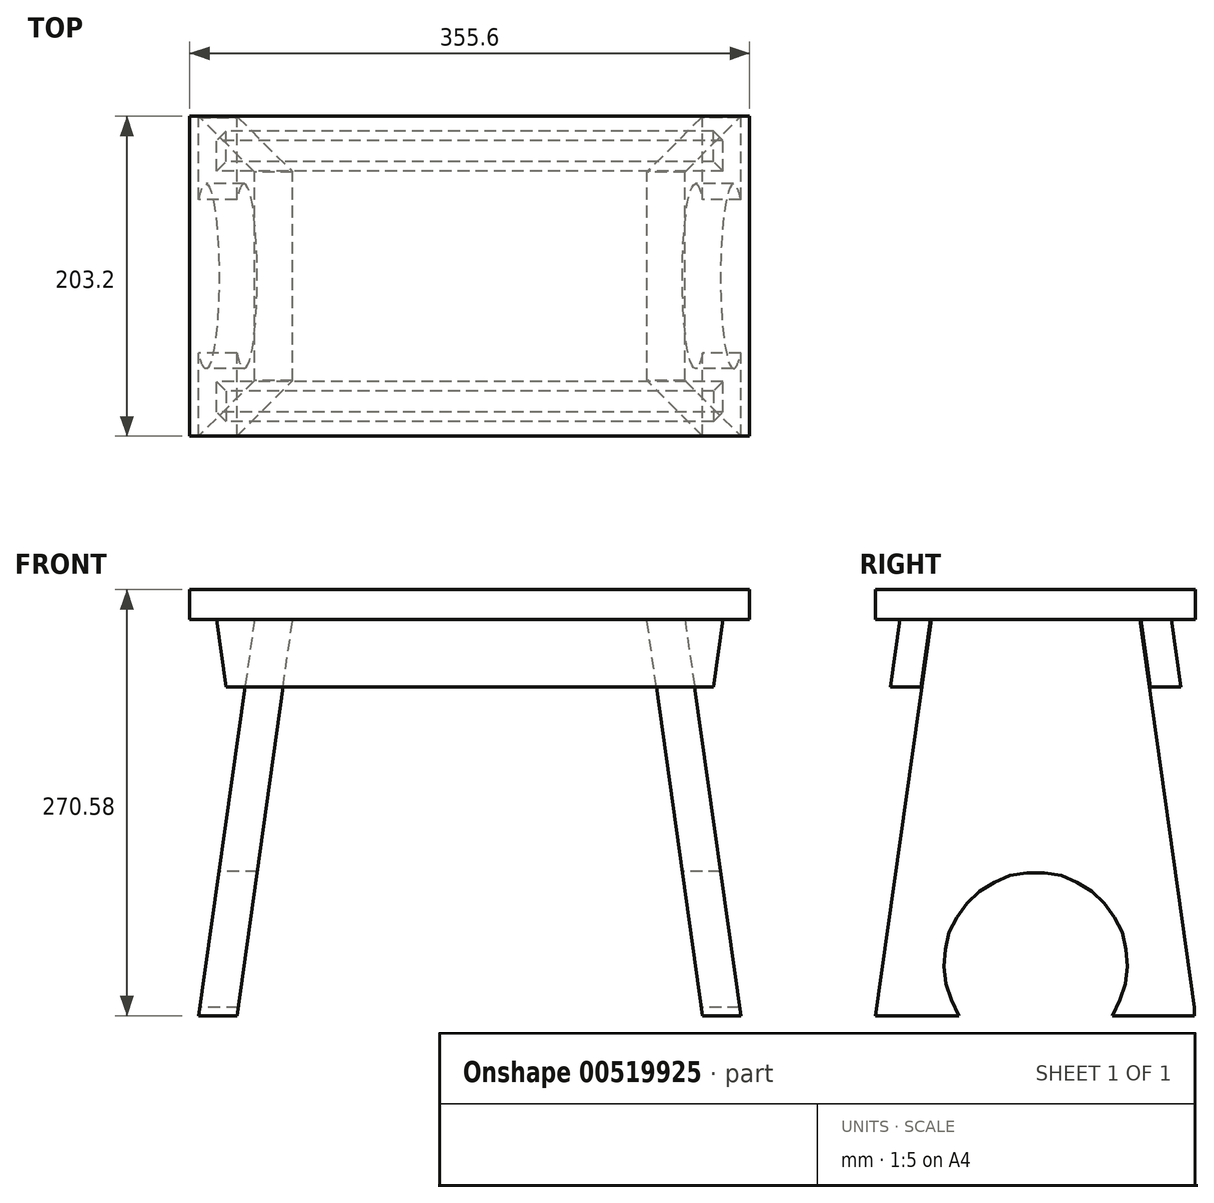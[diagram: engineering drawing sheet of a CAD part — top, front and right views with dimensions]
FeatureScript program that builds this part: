
annotation { "Feature Type Name" : "Feature", "Feature Type Description" : "" }
export const myFeature = defineFeature(function(context is Context, id is Id, definition is map)
    precondition{}
    {
        {
            var Q0;
            Q0=qCreatedBy(makeId("Front.planeOp"),FACE);
            var sketch = newSketch(context, id + "F0", { "sketchPlane" : qUnion([Q0])});
            skLineSegment(sketch, "E0.bottom", {"start": v(177.8, 9.53) * mm, "end": v(-177.8, 9.53) * mm});
            skLineSegment(sketch, "E0.top", {"start": v(177.8, -9.53) * mm, "end": v(-177.8, -9.53) * mm});
            skLineSegment(sketch, "E0.left", {"start": v(177.8, 9.53) * mm, "end": v(177.8, -9.53) * mm});
            skLineSegment(sketch, "E0.right", {"start": v(-177.8, 9.53) * mm, "end": v(-177.8, -9.53) * mm});
            skPoint(sketch, "E0.middle", {"position": v(0, 0) * mm});
            skLineSegment(sketch, "E1.bottom", {"start": v(-177.8, -9.52) * mm, "end": v(177.8, -9.52) * mm, "construction": true});
            skLineSegment(sketch, "E1.top", {"start": v(-177.8, -261.05) * mm, "end": v(177.8, -261.05) * mm, "construction": true});
            skLineSegment(sketch, "E1.left", {"start": v(-177.8, -9.53) * mm, "end": v(-177.8, -261.05) * mm, "construction": true});
            skLineSegment(sketch, "E1.right", {"start": v(177.8, -9.53) * mm, "end": v(177.8, -261.05) * mm, "construction": true});
            skLineSegment(sketch, "E2", {"start": v(136.74, -9.52) * mm, "end": v(172.1, -261.05) * mm});
            skLineSegment(sketch, "E3", {"start": v(172.1, -261.05) * mm, "end": v(147.88, -261.05) * mm});
            skLineSegment(sketch, "E4", {"start": v(147.88, -261.05) * mm, "end": v(112.53, -9.52) * mm});
            skLineSegment(sketch, "E5", {"start": v(112.53, -9.52) * mm, "end": v(136.74, -9.52) * mm});
            skLineSegment(sketch, "E6", {"start": v(0, 0) * mm, "end": v(0, -261.05) * mm, "construction": true});
            skLineSegment(sketch, "E7.MirrorCS", {"start": v(-112.53, -9.52) * mm, "end": v(-136.74, -9.52) * mm});
            skLineSegment(sketch, "E8.MirrorCS", {"start": v(-147.88, -261.05) * mm, "end": v(-112.53, -9.52) * mm});
            skLineSegment(sketch, "E9.MirrorCS", {"start": v(-172.1, -261.05) * mm, "end": v(-147.88, -261.05) * mm});
            skLineSegment(sketch, "E10.MirrorCS", {"start": v(-136.74, -9.52) * mm, "end": v(-172.1, -261.05) * mm});
            skLineSegment(sketch, "E11.bottom", {"start": v(-177.8, -9.53) * mm, "end": v(177.8, -9.53) * mm});
            skLineSegment(sketch, "E11.top", {"start": v(-177.8, -52.5) * mm, "end": v(177.8, -52.5) * mm});
            skLineSegment(sketch, "E11.left", {"start": v(-177.8, -9.53) * mm, "end": v(-177.8, -52.5) * mm});
            skLineSegment(sketch, "E11.right", {"start": v(177.8, -9.53) * mm, "end": v(177.8, -52.5) * mm});
            skLineSegment(sketch, "E12", {"start": v(160.78, -9.52) * mm, "end": v(154.74, -52.5) * mm});
            skLineSegment(sketch, "E13.MirrorCS", {"start": v(-160.78, -9.52) * mm, "end": v(-154.74, -52.5) * mm});
            skSolve(sketch);
        }
        {
            var Q0;
            Q0=makeQuery(id+"F0.imprint","IMPRINT",FACE,{"disambiguationData":[TD([[makeQuery(id+"F0.imprint","IMPRINT",EDGE,{"derivedFrom":sQuery(id+"F0.wireOp",EDGE,"E0.bottom")}),1.0]])]});
            extrude(context, id + "F1", {"entities" : qUnion([Q0]), "endBound" : BoundingType.SYMMETRIC, "depth" : 203.2 * mm, "offsetDistance" : 25.4 * mm});
        }
        {
            var Q0;
            {var subQ0=sQuery(id+"F0.wireOp",EDGE,"E9.MirrorCS");Q0=makeQuery(id+"F0.imprint","IMPRINT",FACE,{"disambiguationData":[TD([[makeQuery(id+"F0.imprint","IMPRINT",EDGE,{"derivedFrom":subQ0}),1.0]])]});}
            var Q1;
            {var subQ0=sQuery(id+"F0.wireOp",EDGE,"E11.bottom");var subQ1=sQuery(id+"F0.wireOp",EDGE,"E8.MirrorCS");var subQ2=makeQuery(id+"F0.imprint","INTERSECT",VERTEX,{"derivedFrom":[subQ1,subQ0]});Q1=makeQuery(id+"F0.imprint","IMPRINT",FACE,{"disambiguationData":[TD([[makeQuery(id+"F0.imprint","IMPRINT",EDGE,{"disambiguationData":[TD([[subQ2,1.0]])],"derivedFrom":subQ1}),1.0]])]});}
            var Q2;
            {var subQ0=sQuery(id+"F0.wireOp",EDGE,"E11.bottom");var subQ1=sQuery(id+"F0.wireOp",EDGE,"E2");var subQ2=makeQuery(id+"F0.imprint","INTERSECT",VERTEX,{"derivedFrom":[subQ1,subQ0]});Q2=makeQuery(id+"F0.imprint","IMPRINT",FACE,{"disambiguationData":[TD([[makeQuery(id+"F0.imprint","IMPRINT",EDGE,{"disambiguationData":[TD([[subQ2,-1.0]])],"derivedFrom":subQ1}),-1.0]])]});}
            var Q3;
            {var subQ0=sQuery(id+"F0.wireOp",EDGE,"E3");Q3=makeQuery(id+"F0.imprint","IMPRINT",FACE,{"disambiguationData":[TD([[makeQuery(id+"F0.imprint","IMPRINT",EDGE,{"derivedFrom":subQ0}),-1.0]])]});}
            var Q4;
            Q4=makeQuery(id+"F1.opExtrude","CAP_VERTEX",VERTEX,{"disambiguationData":[OSD([sQuery(id+"F0.wireOp",EDGE,"E0.right"),sQuery(id+"F0.wireOp",EDGE,"E11.bottom"),sQuery(id+"F0.wireOp",EDGE,"E11.left")])],"isStart":false});
            extrude(context, id + "F2", {"entities" : qUnion([Q0, Q1, Q2, Q3]), "endBound" : BoundingType.UP_TO_VERTEX, "depth" : 25.4 * mm, "endBoundEntityVertex" : qUnion([Q4]), "offsetDistance" : 25.4 * mm, "hasSecondDirection" : true, "secondDirectionOppositeDirection" : true, "secondDirectionDepth" : 100.84 * mm});
        }
        {
            var Q0;
            Q0=qCreatedBy(makeId("Right.planeOp"),FACE);
            var sketch = newSketch(context, id + "F3", { "sketchPlane" : qUnion([Q0])});
            skLineSegment(sketch, "E14.0.0", {"start": v(100.84, -9.53) * mm, "end": v(-101.6, -9.53) * mm});
            skLineSegment(sketch, "E14.0.1", {"start": v(-101.6, -9.52) * mm, "end": v(-101.6, -261.05) * mm});
            skLineSegment(sketch, "E14.0.2", {"start": v(-101.6, -261.05) * mm, "end": v(100.84, -261.05) * mm});
            skLineSegment(sketch, "E14.0.3", {"start": v(100.84, -261.05) * mm, "end": v(100.84, -9.53) * mm});
            skLineSegment(sketch, "E15", {"start": v(-101.6, -261.05) * mm, "end": v(-66.25, -9.52) * mm});
            skLineSegment(sketch, "E16.MirrorCS", {"start": v(101.6, -261.05) * mm, "end": v(66.25, -9.52) * mm});
            skArc(sketch, "E17", {"start": v(48.74, -261.05) * mm, "mid": v(0, -169.44) * mm, "end": v(-48.74, -261.05) * mm});
            skSolve(sketch);
        }
        {
            var Q0;
            {var subQ0=sQuery(id+"F3.wireOp",EDGE,"E14.0.3");var subQ1=sQuery(id+"F3.wireOp",EDGE,"E14.0.0");var subQ2=makeQuery(id+"F3.imprint","INTERSECT",VERTEX,{"derivedFrom":[subQ1,subQ0]});Q0=makeQuery(id+"F3.imprint","IMPRINT",FACE,{"disambiguationData":[TD([[makeQuery(id+"F3.imprint","IMPRINT",EDGE,{"disambiguationData":[TD([[subQ2,-1.0]])],"derivedFrom":subQ1}),1.0]])]});}
            var Q1;
            {var subQ0=sQuery(id+"F3.wireOp",EDGE,"E14.0.1");Q1=makeQuery(id+"F3.imprint","IMPRINT",FACE,{"disambiguationData":[TD([[makeQuery(id+"F3.imprint","IMPRINT",EDGE,{"derivedFrom":subQ0}),1.0]])]});}
            var Q2;
            {var subQ0=sQuery(id+"F3.wireOp",EDGE,"E17");Q2=makeQuery(id+"F3.imprint","IMPRINT",FACE,{"disambiguationData":[TD([[makeQuery(id+"F3.imprint","IMPRINT",EDGE,{"derivedFrom":subQ0}),1.0]])]});}
            extrude(context, id + "F4", {"entities" : qUnion([Q0, Q1, Q2]), "operationType" : NewBodyOperationType.REMOVE, "endBound" : BoundingType.THROUGH_ALL, "depth" : 25.4 * mm, "offsetDistance" : 25.4 * mm, "hasSecondDirection" : true, "secondDirectionBound" : SecondDirectionBoundingType.THROUGH_ALL, "secondDirectionOppositeDirection" : true, "secondDirectionDepth" : 25.4 * mm});
        }
        {
            var Q0;
            Q0=qCreatedBy(makeId("Right.planeOp"),FACE);
            var sketch = newSketch(context, id + "F5", { "sketchPlane" : qUnion([Q0])});
            skLineSegment(sketch, "E18.0.0", {"start": v(100.84, -261.05) * mm, "end": v(100.84, -255.63) * mm, "construction": true});
            skLineSegment(sketch, "E18.0.1", {"start": v(100.84, -255.63) * mm, "end": v(66.25, -9.52) * mm, "construction": true});
            skLineSegment(sketch, "E18.0.2", {"start": v(66.25, -9.53) * mm, "end": v(-66.25, -9.53) * mm, "construction": true});
            skLineSegment(sketch, "E18.0.3", {"start": v(-66.25, -9.52) * mm, "end": v(-101.6, -261.05) * mm, "construction": true});
            skLineSegment(sketch, "E18.0.4", {"start": v(-101.6, -261.05) * mm, "end": v(-48.74, -261.05) * mm, "construction": true});
            skArc(sketch, "E18.0.5", {"start": v(-48.74, -261.05) * mm, "mid": v(0, -169.44) * mm, "end": v(48.74, -261.05) * mm, "construction": true});
            skLineSegment(sketch, "E18.0.6", {"start": v(48.74, -261.05) * mm, "end": v(100.84, -261.05) * mm, "construction": true});
            skLineSegment(sketch, "E19", {"start": v(-66.91, -9.52) * mm, "end": v(-72.91, -52.21) * mm});
            skLineSegment(sketch, "E20", {"start": v(-72.91, -52.21) * mm, "end": v(-92.15, -52.21) * mm});
            skLineSegment(sketch, "E21", {"start": v(-92.15, -52.21) * mm, "end": v(-86.15, -9.52) * mm});
            skLineSegment(sketch, "E22", {"start": v(-86.15, -9.53) * mm, "end": v(-66.91, -9.53) * mm});
            skLineSegment(sketch, "E23", {"start": v(0, -9.53) * mm, "end": v(0, -196.01) * mm});
            skLineSegment(sketch, "E24.MirrorCS", {"start": v(72.91, -52.21) * mm, "end": v(92.15, -52.21) * mm});
            skLineSegment(sketch, "E25.MirrorCS", {"start": v(92.15, -52.21) * mm, "end": v(86.15, -9.52) * mm});
            skLineSegment(sketch, "E26.MirrorCS", {"start": v(86.15, -9.53) * mm, "end": v(66.91, -9.53) * mm});
            skLineSegment(sketch, "E27.MirrorCS", {"start": v(66.91, -9.52) * mm, "end": v(72.91, -52.21) * mm});
            skLineSegment(sketch, "E28", {"start": v(72.91, -52.21) * mm, "end": v(0, -52.66) * mm});
            skLineSegment(sketch, "E29", {"start": v(0, -52.66) * mm, "end": v(72.91, -52.21) * mm});
            skSolve(sketch);
        }
        {
            var Q0;
            {var subQ0=sQuery(id+"F0.wireOp",EDGE,"E11.right");Q0=makeQuery(id+"F0.imprint","IMPRINT",FACE,{"disambiguationData":[TD([[makeQuery(id+"F0.imprint","IMPRINT",EDGE,{"derivedFrom":subQ0}),-1.0]])]});}
            extrude(context, id + "F6", {"entities" : qUnion([Q0]), "operationType" : NewBodyOperationType.REMOVE, "endBound" : BoundingType.THROUGH_ALL, "depth" : 25.4 * mm, "offsetDistance" : 25.4 * mm, "hasSecondDirection" : true, "secondDirectionBound" : SecondDirectionBoundingType.THROUGH_ALL, "secondDirectionOppositeDirection" : true, "secondDirectionDepth" : 25.4 * mm});
        }
        {
            var Q0;
            {var subQ0=sQuery(id+"F0.wireOp",EDGE,"E11.left");Q0=makeQuery(id+"F0.imprint","IMPRINT",FACE,{"disambiguationData":[TD([[makeQuery(id+"F0.imprint","IMPRINT",EDGE,{"derivedFrom":subQ0}),1.0]])]});}
            extrude(context, id + "F7", {"entities" : qUnion([Q0]), "operationType" : NewBodyOperationType.REMOVE, "endBound" : BoundingType.THROUGH_ALL, "depth" : 25.4 * mm, "offsetDistance" : 25.4 * mm, "hasSecondDirection" : true, "secondDirectionBound" : SecondDirectionBoundingType.THROUGH_ALL, "secondDirectionOppositeDirection" : true, "secondDirectionDepth" : 25.4 * mm});
        }
        {
            var Q0;
            Q0=makeQuery(id+"F5.imprint","IMPRINT",FACE,{"disambiguationData":[TD([[makeQuery(id+"F5.imprint","IMPRINT",EDGE,{"derivedFrom":sQuery(id+"F5.wireOp",EDGE,"E19")}),-1.0]])]});
            var Q1;
            Q1 = qSketchRegion(id + "FKmkBbVp9opvmPy_5", true);
            extrude(context, id + "F8", {"entities" : qUnion([Q0, Q1]), "depth" : 161.8 * mm, "offsetDistance" : 25.4 * mm, "hasSecondDirection" : true, "secondDirectionOppositeDirection" : true, "secondDirectionDepth" : 161.8 * mm});
        }
        {
            var Q0;
            Q0=makeQuery(id+"F5.imprint","IMPRINT",FACE,{"disambiguationData":[TD([[makeQuery(id+"F5.imprint","IMPRINT",EDGE,{"derivedFrom":sQuery(id+"F5.wireOp",EDGE,"E24.MirrorCS")}),1.0]])]});
            extrude(context, id + "F9", {"entities" : qUnion([Q0]), "depth" : 161.8 * mm, "offsetDistance" : 25.4 * mm, "hasSecondDirection" : true, "secondDirectionOppositeDirection" : true, "secondDirectionDepth" : 161.8 * mm});
        }
        {
            var Q0;
            {var subQ0=sQuery(id+"F0.wireOp",EDGE,"E11.right");Q0=makeQuery(id+"F0.imprint","IMPRINT",FACE,{"disambiguationData":[TD([[makeQuery(id+"F0.imprint","IMPRINT",EDGE,{"derivedFrom":subQ0}),-1.0]])]});}
            var Q1;
            {var subQ0=sQuery(id+"F0.wireOp",EDGE,"E11.left");Q1=makeQuery(id+"F0.imprint","IMPRINT",FACE,{"disambiguationData":[TD([[makeQuery(id+"F0.imprint","IMPRINT",EDGE,{"derivedFrom":subQ0}),1.0]])]});}
            extrude(context, id + "F10", {"entities" : qUnion([Q0, Q1]), "operationType" : NewBodyOperationType.REMOVE, "endBound" : BoundingType.THROUGH_ALL, "depth" : 25.4 * mm, "offsetDistance" : 25.4 * mm, "hasSecondDirection" : true, "secondDirectionBound" : SecondDirectionBoundingType.THROUGH_ALL, "secondDirectionOppositeDirection" : true, "secondDirectionDepth" : 25.4 * mm});
        }
        {
            var Q0;
            Q0=makeQuery(id+"F2.opExtrude","SWEPT_BODY",BODY,{"disambiguationData":[OSD([sQuery(id+"F0.wireOp",EDGE,"E8.MirrorCS"),sQuery(id+"F0.wireOp",EDGE,"E9.MirrorCS"),sQuery(id+"F0.wireOp",EDGE,"E10.MirrorCS"),sQuery(id+"F0.wireOp",EDGE,"E11.bottom")])]});
            var Q1;
            Q1=makeQuery(id+"F2.opExtrude","SWEPT_BODY",BODY,{"disambiguationData":[OSD([sQuery(id+"F0.wireOp",EDGE,"E2"),sQuery(id+"F0.wireOp",EDGE,"E3"),sQuery(id+"F0.wireOp",EDGE,"E4"),sQuery(id+"F0.wireOp",EDGE,"E11.bottom")])]});
            var Q2;
            Q2=makeQuery(id+"F9.opExtrude","SWEPT_BODY",BODY,{"disambiguationData":[OSD([sQuery(id+"F5.wireOp",EDGE,"E24.MirrorCS"),sQuery(id+"F5.wireOp",EDGE,"E25.MirrorCS"),sQuery(id+"F5.wireOp",EDGE,"E26.MirrorCS"),sQuery(id+"F5.wireOp",EDGE,"E27.MirrorCS")])]});
            var Q3;
            Q3=makeQuery(id+"F8.opExtrude","SWEPT_BODY",BODY,{"disambiguationData":[OSD([sQuery(id+"F5.wireOp",EDGE,"E19"),sQuery(id+"F5.wireOp",EDGE,"E20"),sQuery(id+"F5.wireOp",EDGE,"E21"),sQuery(id+"F5.wireOp",EDGE,"E22")])]});
            booleanBodies(context, id + "F11", {"operationType" : BooleanOperationType.SUBTRACTION, "tools" : qUnion([Q0, Q1]), "targets" : qUnion([Q2, Q3]), "keepTools" : true});
        }
    });
